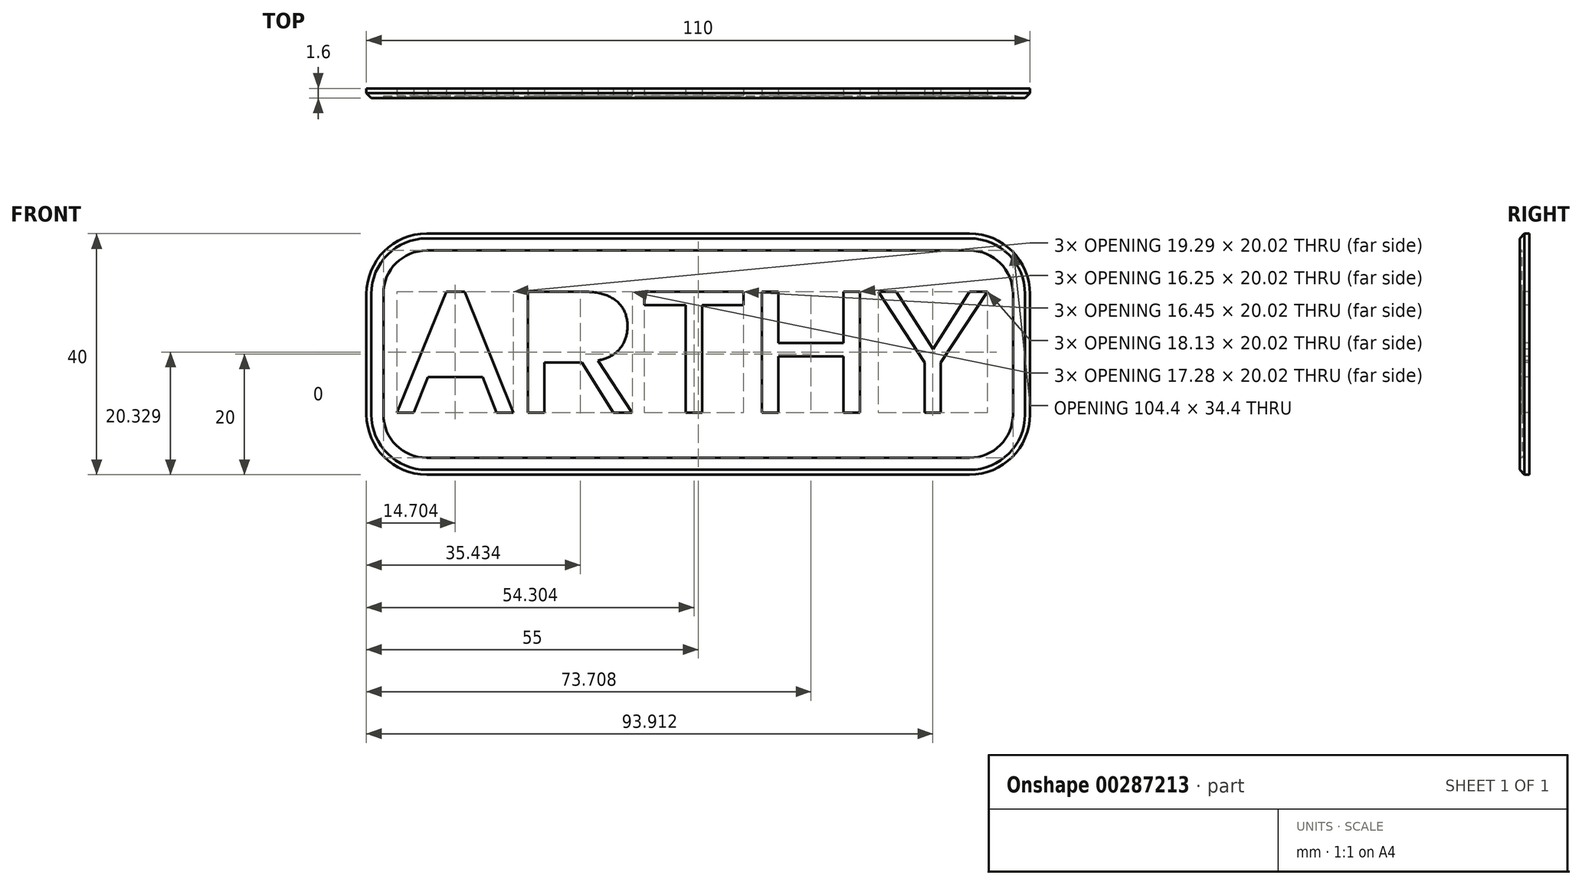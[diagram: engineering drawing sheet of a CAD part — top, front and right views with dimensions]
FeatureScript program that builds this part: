
annotation { "Feature Type Name" : "Feature", "Feature Type Description" : "" }
export const myFeature = defineFeature(function(context is Context, id is Id, definition is map)
    precondition{}
    {
        {
            var Q0;
            Q0=qCreatedBy(makeId("Front.planeOp"),FACE);
            var sketch = newSketch(context, id + "F0", { "sketchPlane" : qUnion([Q0])});
            skLineSegment(sketch, "E0.bottom", {"start": v(-55, 20) * mm, "end": v(55, 20) * mm});
            skLineSegment(sketch, "E0.top", {"start": v(-55, -20) * mm, "end": v(55, -20) * mm});
            skLineSegment(sketch, "E0.left", {"start": v(-55, 20) * mm, "end": v(-55, -20) * mm});
            skLineSegment(sketch, "E0.right", {"start": v(55, 20) * mm, "end": v(55, -20) * mm});
            skSolve(sketch);
        }
        {
            var Q0;
            Q0=qSketchRegion(id+"F0",true);
            extrude(context, id + "F1", {"entities" : qUnion([Q0]), "depth" : 1.6 * mm});
        }
        {
            var Q0;
            Q0=makeQuery(id+"F1.opExtrude","CAP_FACE",FACE,{"disambiguationData":[OSD([sQuery(id+"F0.wireOp",EDGE,"E0.bottom"),sQuery(id+"F0.wireOp",EDGE,"E0.top"),sQuery(id+"F0.wireOp",EDGE,"E0.left"),sQuery(id+"F0.wireOp",EDGE,"E0.right")])],"isStart":false});
            var sketch = newSketch(context, id + "F2", { "sketchPlane" : qUnion([Q0])});
            skText(sketch, "E1", { "text": "ARTHY", "fontName": "Arimo-Regular.ttf"});
            const initialGuessF2  = {"E1": [-0.05, -0.00968, 1, 0, 0.02095]};
            skSetInitialGuess(sketch, initialGuessF2);
            skSolve(sketch);
        }
        {
            var Q0;
            Q0=qSketchRegion(id+"F2",true);
            extrude(context, id + "F3", {"entities" : qUnion([Q0]), "operationType" : NewBodyOperationType.REMOVE, "endBound" : BoundingType.THROUGH_ALL, "oppositeDirection" : true, "depth" : 25 * mm});
        }
        {
            var Q0;
            Q0=makeQuery(id+"F1.opExtrude","SWEPT_EDGE",EDGE,{"disambiguationData":[OSD([sQuery(id+"F0.wireOp",EDGE,"E0.top"),sQuery(id+"F0.wireOp",EDGE,"E0.right")])]});
            var Q1;
            Q1=makeQuery(id+"F1.opExtrude","SWEPT_EDGE",EDGE,{"disambiguationData":[OSD([sQuery(id+"F0.wireOp",EDGE,"E0.bottom"),sQuery(id+"F0.wireOp",EDGE,"E0.right")])]});
            var Q2;
            Q2=makeQuery(id+"F1.opExtrude","SWEPT_EDGE",EDGE,{"disambiguationData":[OSD([sQuery(id+"F0.wireOp",EDGE,"E0.top"),sQuery(id+"F0.wireOp",EDGE,"E0.left")])]});
            var Q3;
            Q3=makeQuery(id+"F1.opExtrude","SWEPT_EDGE",EDGE,{"disambiguationData":[OSD([sQuery(id+"F0.wireOp",EDGE,"E0.bottom"),sQuery(id+"F0.wireOp",EDGE,"E0.left")])]});
            fillet(context, id + "F4", {"entities" : qUnion([Q0, Q1, Q2, Q3]), "radius" : 10 * mm, "tangentPropagation" : true, "allowEdgeOverflow" : false});
        }
        {
            var Q0;
            Q0=makeQuery(id+"F1.opExtrude","CAP_EDGE",EDGE,{"disambiguationData":[OSD([sQuery(id+"F0.wireOp",EDGE,"E0.top")])],"isStart":false});
            chamfer(context, id + "F5", {"entities" : qUnion([Q0]), "width" : 0.8 * mm, "tangentPropagation" : true});
        }
        {
            var Q0;
            Q0=makeQuery(id+"F1.opExtrude","CAP_FACE",FACE,{"disambiguationData":[OSD([sQuery(id+"F0.wireOp",EDGE,"E0.bottom"),sQuery(id+"F0.wireOp",EDGE,"E0.top"),sQuery(id+"F0.wireOp",EDGE,"E0.left"),sQuery(id+"F0.wireOp",EDGE,"E0.right")])],"isStart":false});
            var sketch = newSketch(context, id + "F6", { "sketchPlane" : qUnion([Q0])});
            skLineSegment(sketch, "E2.0", {"start": v(-45, -17.2) * mm, "end": v(45, -17.2) * mm});
            skArc(sketch, "E2.1", {"start": v(-52.2, -10) * mm, "mid": v(-50.1, -15.1) * mm, "end": v(-45, -17.2) * mm});
            skArc(sketch, "E2.2", {"start": v(45, -17.2) * mm, "mid": v(50.1, -15.1) * mm, "end": v(52.2, -10) * mm});
            skLineSegment(sketch, "E2.3", {"start": v(-52.2, 10) * mm, "end": v(-52.2, -10) * mm});
            skLineSegment(sketch, "E2.4", {"start": v(52.2, -10) * mm, "end": v(52.2, 10) * mm});
            skArc(sketch, "E2.5", {"start": v(52.2, 10) * mm, "mid": v(50.1, 15.1) * mm, "end": v(45, 17.2) * mm});
            skLineSegment(sketch, "E2.6", {"start": v(45, 17.2) * mm, "end": v(-45, 17.2) * mm});
            skArc(sketch, "E2.7", {"start": v(-45, 17.2) * mm, "mid": v(-50.1, 15.1) * mm, "end": v(-52.2, 10) * mm});
            skSolve(sketch);
        }
        {
            var Q0;
            Q0=qSketchRegion(id+"F6",true);
            extrude(context, id + "F7", {"entities" : qUnion([Q0]), "operationType" : NewBodyOperationType.REMOVE, "oppositeDirection" : true, "depth" : 0.4 * mm});
        }
        {
            var Q0;
            Q0=makeQuery(id+"F7.boolean.opBoolean","COPY",FACE,{"disambiguationData":[TD([makeQuery(id+"F3.boolean.opBoolean","COPY",FACE,{"derivedFrom":makeQuery(id+"F3.opExtrude","SWEPT_FACE",FACE,{"disambiguationData":[OSD([sQuery(id+"F2.wireOp",EDGE,"E1.sketch_text.stroke-8")])]})})])],"derivedFrom":makeQuery(id+"F7.opExtrude","CAP_FACE",FACE,{"disambiguationData":[OSD([sQuery(id+"F6.wireOp",EDGE,"E2.0"),sQuery(id+"F6.wireOp",EDGE,"E2.1"),sQuery(id+"F6.wireOp",EDGE,"E2.2"),sQuery(id+"F6.wireOp",EDGE,"E2.3"),sQuery(id+"F6.wireOp",EDGE,"E2.4"),sQuery(id+"F6.wireOp",EDGE,"E2.5"),sQuery(id+"F6.wireOp",EDGE,"E2.6"),sQuery(id+"F6.wireOp",EDGE,"E2.7")])],"isStart":false})});
            extrude(context, id + "F8", {"entities" : qUnion([Q0]), "operationType" : NewBodyOperationType.REMOVE, "oppositeDirection" : true, "depth" : 25 * mm});
        }
        {
            var Q0;
            Q0=makeQuery(id+"F7.boolean.opBoolean","COPY",FACE,{"disambiguationData":[TD([makeQuery(id+"F3.boolean.opBoolean","COPY",FACE,{"derivedFrom":makeQuery(id+"F3.opExtrude","SWEPT_FACE",FACE,{"disambiguationData":[OSD([sQuery(id+"F2.wireOp",EDGE,"E1.sketch_text.stroke-27")])]})})])],"derivedFrom":makeQuery(id+"F7.opExtrude","CAP_FACE",FACE,{"disambiguationData":[OSD([sQuery(id+"F6.wireOp",EDGE,"E2.0"),sQuery(id+"F6.wireOp",EDGE,"E2.1"),sQuery(id+"F6.wireOp",EDGE,"E2.2"),sQuery(id+"F6.wireOp",EDGE,"E2.3"),sQuery(id+"F6.wireOp",EDGE,"E2.4"),sQuery(id+"F6.wireOp",EDGE,"E2.5"),sQuery(id+"F6.wireOp",EDGE,"E2.6"),sQuery(id+"F6.wireOp",EDGE,"E2.7")])],"isStart":false})});
            extrude(context, id + "F9", {"entities" : qUnion([Q0]), "operationType" : NewBodyOperationType.REMOVE, "oppositeDirection" : true, "depth" : 25 * mm});
        }
    });
